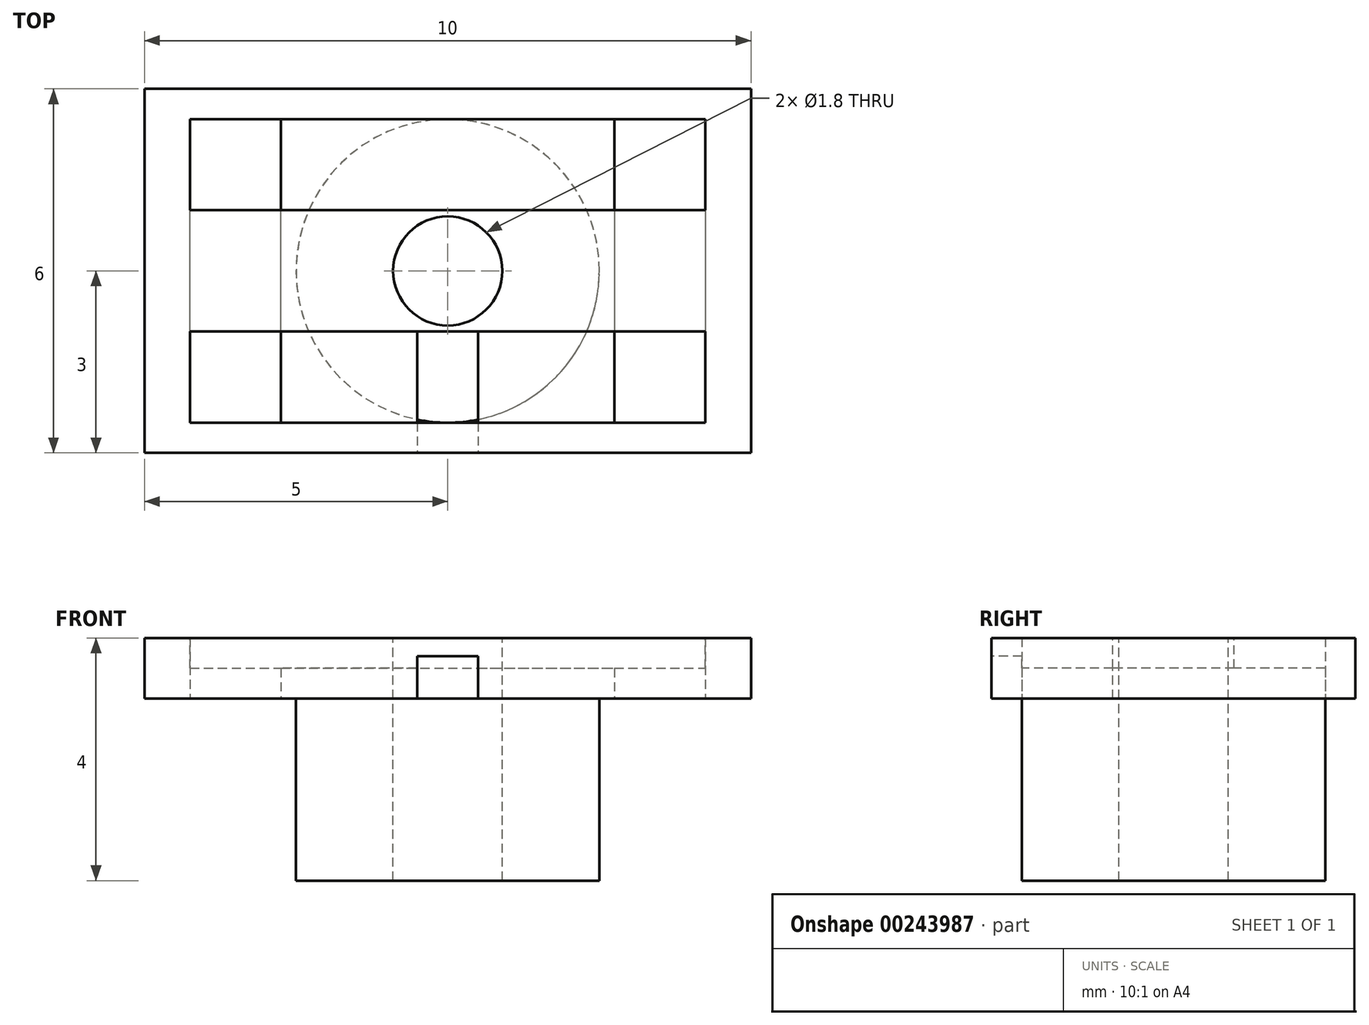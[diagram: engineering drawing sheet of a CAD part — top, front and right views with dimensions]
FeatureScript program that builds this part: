
annotation { "Feature Type Name" : "Feature", "Feature Type Description" : "" }
export const myFeature = defineFeature(function(context is Context, id is Id, definition is map)
    precondition{}
    {
        {
            var Q0;
            Q0=qCreatedBy(makeId("Top.planeOp"),FACE);
            var sketch = newSketch(context, id + "F0", { "sketchPlane" : qUnion([Q0])});
            skLineSegment(sketch, "E0.bottom", {"start": v(-5, -3) * mm, "end": v(5, -3) * mm});
            skLineSegment(sketch, "E0.top", {"start": v(-5, 3) * mm, "end": v(5, 3) * mm});
            skLineSegment(sketch, "E0.left", {"start": v(-5, -3) * mm, "end": v(-5, 3) * mm});
            skLineSegment(sketch, "E0.right", {"start": v(5, -3) * mm, "end": v(5, 3) * mm});
            skPoint(sketch, "E0.middle", {"position": v(0, 0) * mm});
            skLineSegment(sketch, "E1.bottom", {"start": v(-2.75, -2.5) * mm, "end": v(-4.25, -2.5) * mm});
            skLineSegment(sketch, "E1.top", {"start": v(-2.75, 2.5) * mm, "end": v(-4.25, 2.5) * mm});
            skLineSegment(sketch, "E1.left", {"start": v(-2.75, -2.5) * mm, "end": v(-2.75, 2.5) * mm});
            skLineSegment(sketch, "E1.right", {"start": v(-4.25, -2.5) * mm, "end": v(-4.25, 2.5) * mm});
            skPoint(sketch, "E1.middle", {"position": v(-3.5, 0) * mm});
            skLineSegment(sketch, "E2.bottom", {"start": v(2.75, 2.5) * mm, "end": v(4.25, 2.5) * mm});
            skLineSegment(sketch, "E2.top", {"start": v(2.75, -2.5) * mm, "end": v(4.25, -2.5) * mm});
            skLineSegment(sketch, "E2.left", {"start": v(2.75, 2.5) * mm, "end": v(2.75, -2.5) * mm});
            skLineSegment(sketch, "E2.right", {"start": v(4.25, 2.5) * mm, "end": v(4.25, -2.5) * mm});
            skPoint(sketch, "E2.middle", {"position": v(3.5, 0) * mm});
            skPoint(sketch, "E2.cornerSnap0", {"position": v(-3.5, 2.5) * mm});
            skSolve(sketch);
        }
        {
            var Q0;
            Q0=makeQuery(id+"F0.imprint","IMPRINT",FACE,{"disambiguationData":[TD([[makeQuery(id+"F0.imprint","IMPRINT",EDGE,{"derivedFrom":sQuery(id+"F0.wireOp",EDGE,"E0.bottom")}),1.0]])]});
            extrude(context, id + "F1", {"entities" : qUnion([Q0]), "depth" : 0.5 * mm});
        }
        {
            var Q0;
            Q0=makeQuery(id+"F1.opExtrude","CAP_FACE",FACE,{"disambiguationData":[OSD([sQuery(id+"F0.wireOp",EDGE,"E0.bottom"),sQuery(id+"F0.wireOp",EDGE,"E0.top"),sQuery(id+"F0.wireOp",EDGE,"E0.left"),sQuery(id+"F0.wireOp",EDGE,"E0.right"),sQuery(id+"F0.wireOp",EDGE,"E1.bottom"),sQuery(id+"F0.wireOp",EDGE,"E1.top"),sQuery(id+"F0.wireOp",EDGE,"E1.left"),sQuery(id+"F0.wireOp",EDGE,"E1.right"),sQuery(id+"F0.wireOp",EDGE,"E2.bottom"),sQuery(id+"F0.wireOp",EDGE,"E2.top"),sQuery(id+"F0.wireOp",EDGE,"E2.left"),sQuery(id+"F0.wireOp",EDGE,"E2.right")])],"isStart":false});
            var sketch = newSketch(context, id + "F2", { "sketchPlane" : qUnion([Q0])});
            skLineSegment(sketch, "E3.bottom", {"start": v(-5, 3) * mm, "end": v(5, 3) * mm});
            skLineSegment(sketch, "E3.top", {"start": v(-5, -3) * mm, "end": v(5, -3) * mm});
            skLineSegment(sketch, "E3.left", {"start": v(-5, 3) * mm, "end": v(-5, -3) * mm});
            skLineSegment(sketch, "E3.right", {"start": v(5, 3) * mm, "end": v(5, -3) * mm});
            skSolve(sketch);
        }
        {
            var Q0;
            Q0 = qSketchRegion(id + "F2", true);
            extrude(context, id + "F3", {"entities" : qUnion([Q0]), "operationType" : NewBodyOperationType.ADD, "depth" : 0.5 * mm});
        }
        {
            var Q0;
            Q0=makeQuery(id+"F3.opExtrude","CAP_FACE",FACE,{"disambiguationData":[OSD([sQuery(id+"F2.wireOp",EDGE,"E3.bottom"),sQuery(id+"F2.wireOp",EDGE,"E3.top"),sQuery(id+"F2.wireOp",EDGE,"E3.left"),sQuery(id+"F2.wireOp",EDGE,"E3.right")])],"isStart":false});
            var sketch = newSketch(context, id + "F4", { "sketchPlane" : qUnion([Q0])});
            skLineSegment(sketch, "E4.0", {"start": v(-4.25, -2.5) * mm, "end": v(-4.25, 2.5) * mm});
            skLineSegment(sketch, "E5.0", {"start": v(4.25, 2.5) * mm, "end": v(4.25, -2.5) * mm});
            skLineSegment(sketch, "E6.0", {"start": v(-2.75, -2.5) * mm, "end": v(-4.25, -2.5) * mm});
            skLineSegment(sketch, "E7.0", {"start": v(2.75, -2.5) * mm, "end": v(4.25, -2.5) * mm});
            skLineSegment(sketch, "E8.0", {"start": v(-2.75, 2.5) * mm, "end": v(-4.25, 2.5) * mm});
            skLineSegment(sketch, "E9.0", {"start": v(2.75, 2.5) * mm, "end": v(4.25, 2.5) * mm});
            skLineSegment(sketch, "E10.bottom", {"start": v(-4.25, -2.5) * mm, "end": v(4.25, -2.5) * mm});
            skLineSegment(sketch, "E10.top", {"start": v(-4.25, -1) * mm, "end": v(4.25, -1) * mm});
            skLineSegment(sketch, "E10.left", {"start": v(-4.25, -2.5) * mm, "end": v(-4.25, -1) * mm});
            skLineSegment(sketch, "E10.right", {"start": v(4.25, -2.5) * mm, "end": v(4.25, -1) * mm});
            skLineSegment(sketch, "E11.bottom", {"start": v(-4.25, 2.5) * mm, "end": v(4.25, 2.5) * mm});
            skLineSegment(sketch, "E11.top", {"start": v(-4.25, 1) * mm, "end": v(4.25, 1) * mm});
            skLineSegment(sketch, "E11.left", {"start": v(-4.25, 2.5) * mm, "end": v(-4.25, 1) * mm});
            skLineSegment(sketch, "E11.right", {"start": v(4.25, 2.5) * mm, "end": v(4.25, 1) * mm});
            skSolve(sketch);
        }
        {
            var Q0;
            Q0=makeQuery(id+"F4.imprint","IMPRINT",FACE,{"disambiguationData":[TD([[makeQuery(id+"F4.imprint","IMPRINT",EDGE,{"derivedFrom":sQuery(id+"F4.wireOp",EDGE,"E10.top")}),-1.0]])]});
            var Q1;
            Q1=makeQuery(id+"F4.imprint","IMPRINT",FACE,{"disambiguationData":[TD([[makeQuery(id+"F4.imprint","IMPRINT",EDGE,{"derivedFrom":sQuery(id+"F4.wireOp",EDGE,"E11.top")}),1.0]])]});
            extrude(context, id + "F5", {"entities" : qUnion([Q0, Q1]), "operationType" : NewBodyOperationType.REMOVE, "oppositeDirection" : true, "depth" : 0.5 * mm});
        }
        {
            var Q0;
            Q0=makeQuery(id+"F3.boolean.opBoolean","MERGE",FACE,{"derivedFrom":[makeQuery(id+"F1.opExtrude","SWEPT_FACE",FACE,{"disambiguationData":[OSD([sQuery(id+"F0.wireOp",EDGE,"E0.bottom")])]}),makeQuery(id+"F3.opExtrude","SWEPT_FACE",FACE,{"disambiguationData":[OSD([sQuery(id+"F2.wireOp",EDGE,"E3.top")])]})]});
            var sketch = newSketch(context, id + "F6", { "sketchPlane" : qUnion([Q0])});
            skLineSegment(sketch, "E12.bottom", {"start": v(-0.5, 0.7) * mm, "end": v(0.5, 0.7) * mm});
            skLineSegment(sketch, "E12.top", {"start": v(-0.5, 0.2) * mm, "end": v(0.5, 0.2) * mm});
            skLineSegment(sketch, "E12.left", {"start": v(-0.5, 0.7) * mm, "end": v(-0.5, 0.2) * mm});
            skLineSegment(sketch, "E12.right", {"start": v(0.5, 0.7) * mm, "end": v(0.5, 0.2) * mm});
            skSolve(sketch);
        }
        {
            var Q0;
            Q0 = qSketchRegion(id + "F6", true);
            var Q1;
            Q1=makeQuery(id+"F5.boolean.opBoolean","COPY",FACE,{"derivedFrom":makeQuery(id+"F5.opExtrude","SWEPT_FACE",FACE,{"disambiguationData":[OSD([sQuery(id+"F4.wireOp",EDGE,"E10.top")])]})});
            extrude(context, id + "F7", {"entities" : qUnion([Q0]), "operationType" : NewBodyOperationType.REMOVE, "endBound" : BoundingType.UP_TO_SURFACE, "oppositeDirection" : true, "endBoundEntityFace" : qUnion([Q1]), "depth" : 25 * mm});
        }
        {
            var Q0;
            Q0=makeQuery(id+"F0.imprint","IMPRINT",FACE,{"disambiguationData":[TD([[makeQuery(id+"F0.imprint","IMPRINT",EDGE,{"derivedFrom":sQuery(id+"F0.wireOp",EDGE,"E0.bottom")}),1.0]])]});
            var sketch = newSketch(context, id + "F8", { "sketchPlane" : qUnion([Q0])});
            skCircle(sketch, "E13", {"center": v(0, 0) * mm, "radius": 2.5 * mm});
            skCircle(sketch, "E14", {"center": v(0, 0) * mm, "radius": 0.9 * mm});
            skSolve(sketch);
        }
        {
            var Q0;
            Q0 = qSketchRegion(id + "F8", true);
            extrude(context, id + "F9", {"entities" : qUnion([Q0]), "oppositeDirection" : true, "depth" : 3 * mm});
        }
        {
            var Q0;
            Q0=makeQuery(id+"F3.opExtrude","CAP_FACE",FACE,{"disambiguationData":[OSD([sQuery(id+"F2.wireOp",EDGE,"E3.bottom"),sQuery(id+"F2.wireOp",EDGE,"E3.top"),sQuery(id+"F2.wireOp",EDGE,"E3.left"),sQuery(id+"F2.wireOp",EDGE,"E3.right")])],"isStart":false});
            var sketch = newSketch(context, id + "F10", { "sketchPlane" : qUnion([Q0])});
            skCircle(sketch, "E15.0", {"center": v(0, 0) * mm, "radius": 0.9 * mm});
            skSolve(sketch);
        }
        {
            var Q0;
            Q0 = qSketchRegion(id + "F10", true);
            extrude(context, id + "F11", {"entities" : qUnion([Q0]), "operationType" : NewBodyOperationType.REMOVE, "endBound" : BoundingType.THROUGH_ALL, "oppositeDirection" : true, "depth" : 25 * mm});
        }
        {
            var Q0;
            Q0=makeQuery(id+"F7.boolean.opBoolean","COPY",FACE,{"derivedFrom":makeQuery(id+"F7.opExtrude","SWEPT_FACE",FACE,{"disambiguationData":[OSD([sQuery(id+"F6.wireOp",EDGE,"E12.top")])]})});
            var Q1;
            Q1=makeQuery(id+"F1.opExtrude","CAP_FACE",FACE,{"disambiguationData":[OSD([sQuery(id+"F0.wireOp",EDGE,"E0.bottom"),sQuery(id+"F0.wireOp",EDGE,"E0.top"),sQuery(id+"F0.wireOp",EDGE,"E0.left"),sQuery(id+"F0.wireOp",EDGE,"E0.right"),sQuery(id+"F0.wireOp",EDGE,"E1.bottom"),sQuery(id+"F0.wireOp",EDGE,"E1.top"),sQuery(id+"F0.wireOp",EDGE,"E1.left"),sQuery(id+"F0.wireOp",EDGE,"E1.right"),sQuery(id+"F0.wireOp",EDGE,"E2.bottom"),sQuery(id+"F0.wireOp",EDGE,"E2.top"),sQuery(id+"F0.wireOp",EDGE,"E2.left"),sQuery(id+"F0.wireOp",EDGE,"E2.right")])],"isStart":true});
            extrude(context, id + "F12", {"entities" : qUnion([Q0]), "operationType" : NewBodyOperationType.REMOVE, "endBound" : BoundingType.UP_TO_SURFACE, "oppositeDirection" : true, "endBoundEntityFace" : qUnion([Q1]), "depth" : 25 * mm});
        }
    });
